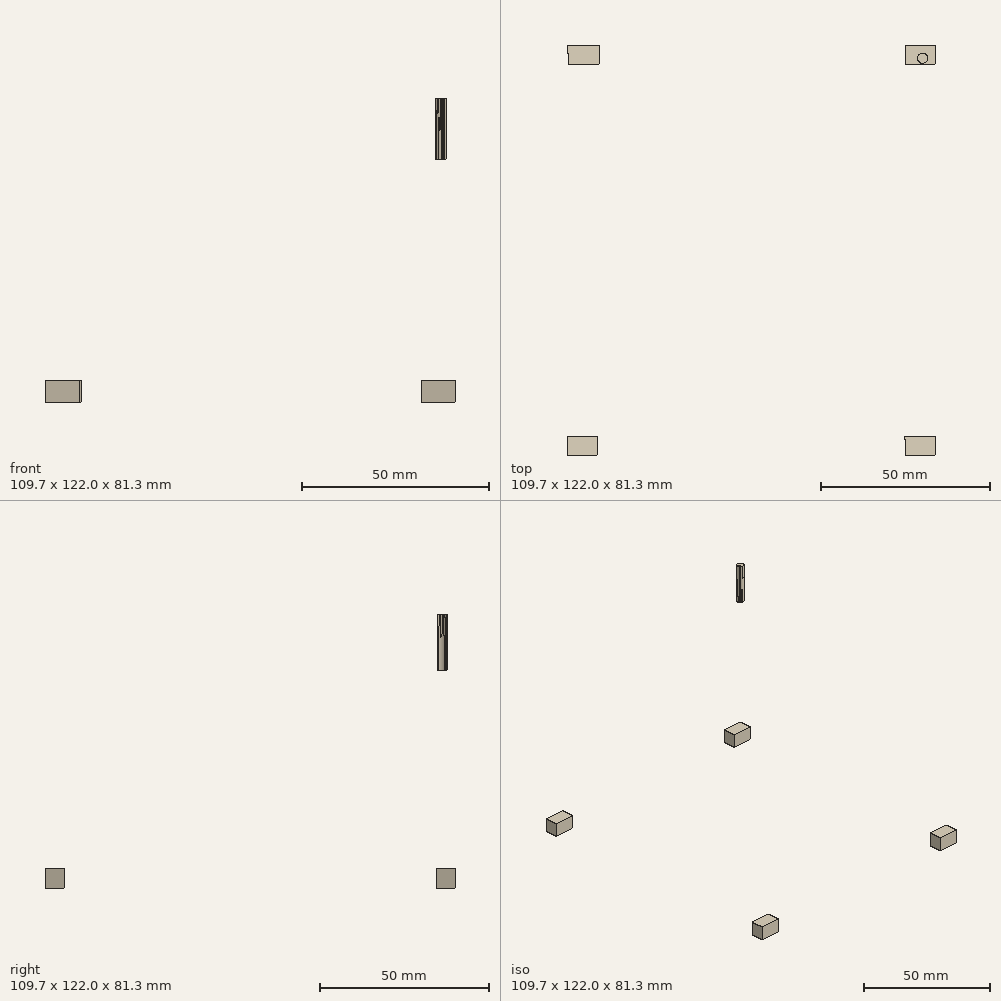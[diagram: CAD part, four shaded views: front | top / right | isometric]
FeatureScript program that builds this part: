
annotation { "Feature Type Name" : "Feature", "Feature Type Description" : "" }
export const myFeature = defineFeature(function(context is Context, id is Id, definition is map)
    precondition{}
    {
        {
            var Q0;
            Q0=qCreatedBy(makeId("Top.planeOp"),FACE);
            var sketch = newSketch(context, id + "F0", { "sketchPlane" : qUnion([Q0])});
            skCircle(sketch, "E0", {"center": v(50.8, 57.15) * mm, "radius": 1.52 * mm});
            skCircle(sketch, "E1", {"center": v(50.8, -57.15) * mm, "radius": 1.52 * mm});
            skCircle(sketch, "E2", {"center": v(-50.8, -57.15) * mm, "radius": 1.52 * mm});
            skCircle(sketch, "E3", {"center": v(-50.8, 57.15) * mm, "radius": 1.52 * mm});
            skLineSegment(sketch, "E4", {"start": v(43.27, 60.96) * mm, "end": v(-43.27, 60.96) * mm});
            skArc(sketch, "E5", {"start": v(43.27, 60.96) * mm, "mid": v(44.49, 60.34) * mm, "end": v(44.72, 59) * mm});
            skArc(sketch, "E6", {"start": v(52.64, 51.07) * mm, "mid": v(46.3, 52.66) * mm, "end": v(44.72, 59) * mm});
            skArc(sketch, "E7", {"start": v(52.64, 51.07) * mm, "mid": v(54, 50.84) * mm, "end": v(54.61, 49.62) * mm});
            skLineSegment(sketch, "E8", {"start": v(54.61, -49.62) * mm, "end": v(54.61, 49.62) * mm});
            skArc(sketch, "E9", {"start": v(54.61, -49.62) * mm, "mid": v(54, -50.84) * mm, "end": v(52.64, -51.07) * mm});
            skArc(sketch, "E10", {"start": v(52.64, -51.07) * mm, "mid": v(46.3, -52.66) * mm, "end": v(44.72, -59) * mm});
            skArc(sketch, "E11", {"start": v(44.72, -59) * mm, "mid": v(44.49, -60.34) * mm, "end": v(43.27, -60.96) * mm});
            skLineSegment(sketch, "E12", {"start": v(-43.27, -60.96) * mm, "end": v(43.27, -60.96) * mm});
            skArc(sketch, "E13", {"start": v(-43.27, -60.96) * mm, "mid": v(-44.49, -60.34) * mm, "end": v(-44.72, -59) * mm});
            skArc(sketch, "E14", {"start": v(-52.64, -51.07) * mm, "mid": v(-46.3, -52.66) * mm, "end": v(-44.72, -59) * mm});
            skArc(sketch, "E15", {"start": v(-52.64, -51.07) * mm, "mid": v(-54, -50.84) * mm, "end": v(-54.61, -49.62) * mm});
            skLineSegment(sketch, "E16", {"start": v(-54.61, 49.62) * mm, "end": v(-54.61, -49.62) * mm});
            skArc(sketch, "E17", {"start": v(-54.61, 49.62) * mm, "mid": v(-54, 50.84) * mm, "end": v(-52.64, 51.07) * mm});
            skArc(sketch, "E18", {"start": v(-52.64, 51.07) * mm, "mid": v(-46.3, 52.66) * mm, "end": v(-44.72, 59) * mm});
            skArc(sketch, "E19", {"start": v(-44.72, 59) * mm, "mid": v(-44.49, 60.34) * mm, "end": v(-43.27, 60.96) * mm});
            skArc(sketch, "E20", {"start": v(57.15, 57.15) * mm, "mid": v(55.3, 61.64) * mm, "end": v(50.8, 63.5) * mm});
            skLineSegment(sketch, "E21", {"start": v(50.8, 63.5) * mm, "end": v(-50.8, 63.5) * mm});
            skArc(sketch, "E22", {"start": v(-50.8, 63.5) * mm, "mid": v(-55.3, 61.64) * mm, "end": v(-57.15, 57.15) * mm});
            skLineSegment(sketch, "E23", {"start": v(-57.15, 57.15) * mm, "end": v(-57.15, -57.15) * mm});
            skArc(sketch, "E24", {"start": v(-57.15, -57.15) * mm, "mid": v(-55.3, -61.64) * mm, "end": v(-50.8, -63.5) * mm});
            skLineSegment(sketch, "E25", {"start": v(-50.8, -63.5) * mm, "end": v(50.8, -63.5) * mm});
            skArc(sketch, "E26", {"start": v(50.8, -63.5) * mm, "mid": v(55.3, -61.64) * mm, "end": v(57.15, -57.15) * mm});
            skLineSegment(sketch, "E27", {"start": v(57.15, -57.15) * mm, "end": v(57.15, 57.15) * mm});
            skSolve(sketch);
        }
        {
            var Q0;
            Q0=makeQuery(id+"F0.imprint","IMPRINT",FACE,{"disambiguationData":[TD([[makeQuery(id+"F0.imprint","IMPRINT",EDGE,{"derivedFrom":sQuery(id+"F0.wireOp",EDGE,"E0")}),1.0]])]});
            extrude(context, id + "F1", {"entities" : qUnion([Q0]), "depth" : 81.28 * mm, "offsetDistance" : 25.4 * mm});
        }
        {
            var Q0;
            Q0=makeQuery(id+"F1.opExtrude","CAP_FACE",FACE,{"disambiguationData":[OSD([sQuery(id+"F0.wireOp",EDGE,"E0"),sQuery(id+"F0.wireOp",EDGE,"E1"),sQuery(id+"F0.wireOp",EDGE,"E2"),sQuery(id+"F0.wireOp",EDGE,"E3"),sQuery(id+"F0.wireOp",EDGE,"E4"),sQuery(id+"F0.wireOp",EDGE,"E5"),sQuery(id+"F0.wireOp",EDGE,"E6"),sQuery(id+"F0.wireOp",EDGE,"E7"),sQuery(id+"F0.wireOp",EDGE,"E8"),sQuery(id+"F0.wireOp",EDGE,"E9"),sQuery(id+"F0.wireOp",EDGE,"E10"),sQuery(id+"F0.wireOp",EDGE,"E11"),sQuery(id+"F0.wireOp",EDGE,"E12"),sQuery(id+"F0.wireOp",EDGE,"E13"),sQuery(id+"F0.wireOp",EDGE,"E14"),sQuery(id+"F0.wireOp",EDGE,"E15"),sQuery(id+"F0.wireOp",EDGE,"E16"),sQuery(id+"F0.wireOp",EDGE,"E17"),sQuery(id+"F0.wireOp",EDGE,"E18"),sQuery(id+"F0.wireOp",EDGE,"E19"),sQuery(id+"F0.wireOp",EDGE,"E20"),sQuery(id+"F0.wireOp",EDGE,"E21"),sQuery(id+"F0.wireOp",EDGE,"E22"),sQuery(id+"F0.wireOp",EDGE,"E23"),sQuery(id+"F0.wireOp",EDGE,"E24"),sQuery(id+"F0.wireOp",EDGE,"E25"),sQuery(id+"F0.wireOp",EDGE,"E26"),sQuery(id+"F0.wireOp",EDGE,"E27")])],"isStart":true});
            var sketch = newSketch(context, id + "F2", { "sketchPlane" : qUnion([Q0])});
            skLineSegment(sketch, "E28.bottom", {"start": v(41.22, 60.96) * mm, "end": v(54.61, 60.96) * mm});
            skLineSegment(sketch, "E28.top", {"start": v(41.22, 43.56) * mm, "end": v(54.61, 43.56) * mm});
            skLineSegment(sketch, "E28.left", {"start": v(41.22, 60.96) * mm, "end": v(41.22, 43.56) * mm});
            skLineSegment(sketch, "E28.right", {"start": v(54.61, 60.96) * mm, "end": v(54.61, 43.56) * mm});
            skLineSegment(sketch, "E29", {"start": v(-54.61, 45.56) * mm, "end": v(-42.43, 46) * mm});
            skLineSegment(sketch, "E30", {"start": v(-42.43, 46) * mm, "end": v(-42.43, 60.96) * mm});
            skLineSegment(sketch, "E31", {"start": v(-42.43, 60.96) * mm, "end": v(-54.61, 60.96) * mm});
            skLineSegment(sketch, "E32", {"start": v(-54.61, 60.96) * mm, "end": v(-54.61, 45.56) * mm});
            skLineSegment(sketch, "E33", {"start": v(37.93, -60.96) * mm, "end": v(37.4, -45.96) * mm});
            skLineSegment(sketch, "E34", {"start": v(37.4, -45.96) * mm, "end": v(54.61, -45.96) * mm});
            skLineSegment(sketch, "E35", {"start": v(54.61, -45.96) * mm, "end": v(54.61, -60.96) * mm});
            skLineSegment(sketch, "E36", {"start": v(54.61, -60.96) * mm, "end": v(37.93, -60.96) * mm});
            skLineSegment(sketch, "E37", {"start": v(-54.61, -47.44) * mm, "end": v(-39.34, -47.44) * mm});
            skLineSegment(sketch, "E38", {"start": v(-39.34, -47.44) * mm, "end": v(-39.34, -60.96) * mm});
            skLineSegment(sketch, "E39", {"start": v(-39.34, -60.96) * mm, "end": v(-54.61, -60.96) * mm});
            skLineSegment(sketch, "E40", {"start": v(-54.61, -60.96) * mm, "end": v(-54.61, -47.44) * mm});
            skSolve(sketch);
        }
        {
            var Q0;
            Q0 = qSketchRegion(id + "F2", true);
            extrude(context, id + "F3", {"entities" : qUnion([Q0]), "operationType" : NewBodyOperationType.REMOVE, "oppositeDirection" : true, "depth" : 64.87 * mm, "offsetDistance" : 25.4 * mm});
        }
        {
            var Q0;
            Q0=qCreatedBy(makeId("Top.planeOp"),FACE);
            var sketch = newSketch(context, id + "F4", { "sketchPlane" : qUnion([Q0])});
            skLineSegment(sketch, "E41", {"start": v(-55, -55.4) * mm, "end": v(-45.88, -55.4) * mm});
            skLineSegment(sketch, "E42", {"start": v(-45.88, -55.4) * mm, "end": v(-45.88, -60.98) * mm});
            skLineSegment(sketch, "E43", {"start": v(-45.88, -60.98) * mm, "end": v(-54.9, -60.98) * mm});
            skLineSegment(sketch, "E44", {"start": v(-54.9, -60.98) * mm, "end": v(-55, -55.4) * mm});
            skLineSegment(sketch, "E45", {"start": v(-54.76, 60.99) * mm, "end": v(-45.5, 60.99) * mm});
            skLineSegment(sketch, "E46", {"start": v(-45.5, 60.99) * mm, "end": v(-45.5, 55.4) * mm});
            skLineSegment(sketch, "E47", {"start": v(-45.5, 55.4) * mm, "end": v(-54.66, 55.4) * mm});
            skLineSegment(sketch, "E48", {"start": v(-54.66, 55.4) * mm, "end": v(-54.76, 60.99) * mm});
            skLineSegment(sketch, "E49", {"start": v(45.62, 60.99) * mm, "end": v(54.74, 60.99) * mm});
            skLineSegment(sketch, "E50", {"start": v(54.74, 60.99) * mm, "end": v(54.74, 55.4) * mm});
            skLineSegment(sketch, "E51", {"start": v(54.74, 55.4) * mm, "end": v(45.72, 55.4) * mm});
            skLineSegment(sketch, "E52", {"start": v(45.72, 55.4) * mm, "end": v(45.62, 60.99) * mm});
            skLineSegment(sketch, "E53", {"start": v(45.51, -55.4) * mm, "end": v(54.64, -55.4) * mm});
            skLineSegment(sketch, "E54", {"start": v(54.64, -55.4) * mm, "end": v(54.64, -60.98) * mm});
            skLineSegment(sketch, "E55", {"start": v(54.64, -60.98) * mm, "end": v(45.62, -60.98) * mm});
            skLineSegment(sketch, "E56", {"start": v(45.62, -60.98) * mm, "end": v(45.51, -55.4) * mm});
            skSolve(sketch);
        }
        {
            var Q0;
            Q0 = qSketchRegion(id + "F4", true);
            extrude(context, id + "F5", {"entities" : qUnion([Q0]), "operationType" : NewBodyOperationType.ADD, "depth" : 5.84 * mm, "offsetDistance" : 25.4 * mm});
        }
    });
